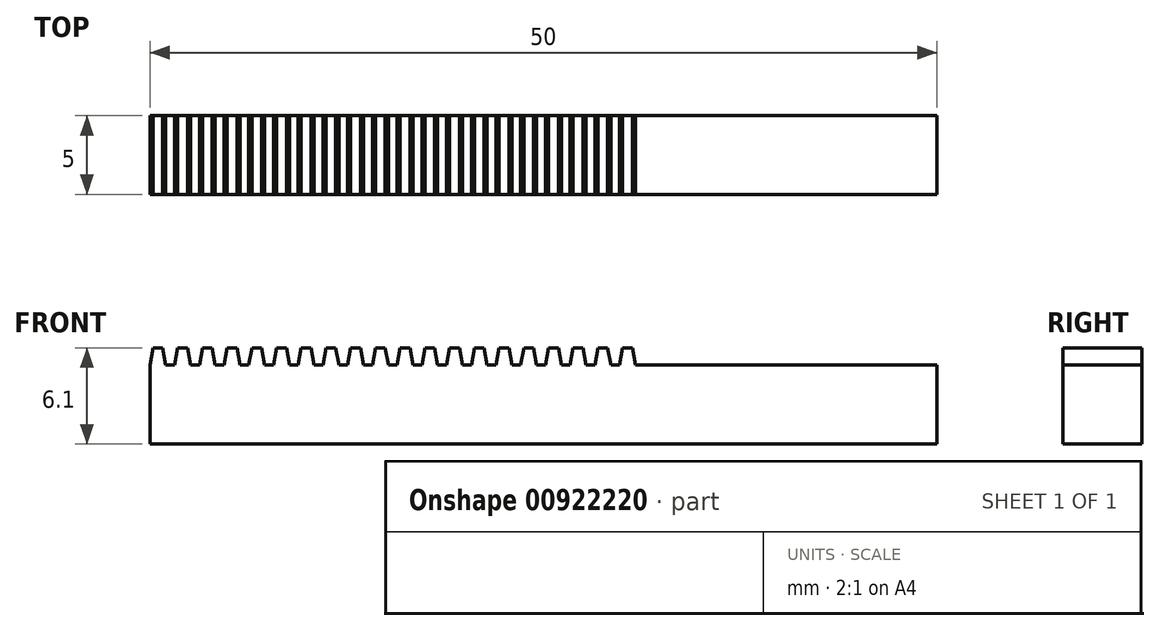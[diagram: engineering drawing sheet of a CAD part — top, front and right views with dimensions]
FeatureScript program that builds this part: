
annotation { "Feature Type Name" : "Feature", "Feature Type Description" : "" }
export const myFeature = defineFeature(function(context is Context, id is Id, definition is map)
    precondition{}
    {
        {
            var Q0;
            Q0=qCreatedBy(makeId("Front.planeOp"),FACE);
            var sketch = newSketch(context, id + "F0", { "sketchPlane" : qUnion([Q0])});
            skLineSegment(sketch, "E0.bottom", {"start": v(0, 0) * mm, "end": v(50, 0) * mm});
            skLineSegment(sketch, "E0.top", {"start": v(0, 5) * mm, "end": v(50, 5) * mm});
            skLineSegment(sketch, "E0.left", {"start": v(0, 0) * mm, "end": v(0, 5) * mm});
            skLineSegment(sketch, "E0.right", {"start": v(50, 0) * mm, "end": v(50, 5) * mm});
            skLineSegment(sketch, "E1", {"start": v(0, 5) * mm, "end": v(1.57, 5) * mm, "construction": true});
            skLineSegment(sketch, "E2", {"start": v(1.57, 5) * mm, "end": v(1.57, 6.1) * mm, "construction": true});
            skLineSegment(sketch, "E3", {"start": v(0, 5) * mm, "end": v(0.2, 6.1) * mm});
            skLineSegment(sketch, "E4", {"start": v(0, 5) * mm, "end": v(1, 5) * mm, "construction": true});
            skLineSegment(sketch, "E5", {"start": v(1, 5) * mm, "end": v(0.82, 6.1) * mm});
            skLineSegment(sketch, "E6", {"start": v(0.2, 6.1) * mm, "end": v(0.82, 6.1) * mm});
            skLineSegment(sketch, "E7.1.0.0", {"start": v(1.57, 5) * mm, "end": v(1.76, 6.1) * mm});
            skLineSegment(sketch, "E7.1.0.1", {"start": v(1.76, 6.1) * mm, "end": v(2.39, 6.1) * mm});
            skLineSegment(sketch, "E7.1.0.2", {"start": v(2.58, 5) * mm, "end": v(2.39, 6.1) * mm});
            skLineSegment(sketch, "E7.2.0.0", {"start": v(3.14, 5) * mm, "end": v(3.33, 6.1) * mm});
            skLineSegment(sketch, "E7.2.0.1", {"start": v(3.33, 6.1) * mm, "end": v(3.96, 6.1) * mm});
            skLineSegment(sketch, "E7.2.0.2", {"start": v(4.15, 5) * mm, "end": v(3.96, 6.1) * mm});
            skLineSegment(sketch, "E8.0.3.0", {"start": v(4.7, 5) * mm, "end": v(4.9, 6.1) * mm});
            skLineSegment(sketch, "E8.3.3.0", {"start": v(4.9, 6.1) * mm, "end": v(5.53, 6.1) * mm});
            skLineSegment(sketch, "E8.6.3.0", {"start": v(5.72, 5) * mm, "end": v(5.53, 6.1) * mm});
            skLineSegment(sketch, "E8.0.4.0", {"start": v(6.28, 5) * mm, "end": v(6.47, 6.1) * mm});
            skLineSegment(sketch, "E8.3.4.0", {"start": v(6.47, 6.1) * mm, "end": v(7.1, 6.1) * mm});
            skLineSegment(sketch, "E8.6.4.0", {"start": v(7.29, 5) * mm, "end": v(7.1, 6.1) * mm});
            skLineSegment(sketch, "E8.0.5.0", {"start": v(7.85, 5) * mm, "end": v(8.04, 6.1) * mm});
            skLineSegment(sketch, "E8.3.5.0", {"start": v(8.04, 6.1) * mm, "end": v(8.67, 6.1) * mm});
            skLineSegment(sketch, "E8.6.5.0", {"start": v(8.86, 5) * mm, "end": v(8.67, 6.1) * mm});
            skLineSegment(sketch, "E8.0.6.0", {"start": v(9.42, 5) * mm, "end": v(9.61, 6.1) * mm});
            skLineSegment(sketch, "E8.3.6.0", {"start": v(9.61, 6.1) * mm, "end": v(10.24, 6.1) * mm});
            skLineSegment(sketch, "E8.6.6.0", {"start": v(10.43, 5) * mm, "end": v(10.24, 6.1) * mm});
            skLineSegment(sketch, "E8.0.7.0", {"start": v(10.99, 5) * mm, "end": v(11.18, 6.1) * mm});
            skLineSegment(sketch, "E8.3.7.0", {"start": v(11.18, 6.1) * mm, "end": v(11.8, 6.1) * mm});
            skLineSegment(sketch, "E8.6.7.0", {"start": v(12, 5) * mm, "end": v(11.8, 6.1) * mm});
            skLineSegment(sketch, "E8.0.8.0", {"start": v(12.56, 5) * mm, "end": v(12.75, 6.1) * mm});
            skLineSegment(sketch, "E8.3.8.0", {"start": v(12.75, 6.1) * mm, "end": v(13.38, 6.1) * mm});
            skLineSegment(sketch, "E8.6.8.0", {"start": v(13.57, 5) * mm, "end": v(13.38, 6.1) * mm});
            skLineSegment(sketch, "E8.0.9.0", {"start": v(14.13, 5) * mm, "end": v(14.32, 6.1) * mm});
            skLineSegment(sketch, "E8.3.9.0", {"start": v(14.32, 6.1) * mm, "end": v(14.95, 6.1) * mm});
            skLineSegment(sketch, "E8.6.9.0", {"start": v(15.14, 5) * mm, "end": v(14.95, 6.1) * mm});
            skLineSegment(sketch, "E8.0.10.0", {"start": v(15.7, 5) * mm, "end": v(15.9, 6.1) * mm});
            skLineSegment(sketch, "E8.3.10.0", {"start": v(15.9, 6.1) * mm, "end": v(16.52, 6.1) * mm});
            skLineSegment(sketch, "E8.6.10.0", {"start": v(16.7, 5) * mm, "end": v(16.52, 6.1) * mm});
            skLineSegment(sketch, "E8.0.11.0", {"start": v(17.27, 5) * mm, "end": v(17.46, 6.1) * mm});
            skLineSegment(sketch, "E8.3.11.0", {"start": v(17.46, 6.1) * mm, "end": v(18.09, 6.1) * mm});
            skLineSegment(sketch, "E8.6.11.0", {"start": v(18.28, 5) * mm, "end": v(18.09, 6.1) * mm});
            skLineSegment(sketch, "E8.0.12.0", {"start": v(18.84, 5) * mm, "end": v(19.03, 6.1) * mm});
            skLineSegment(sketch, "E8.3.12.0", {"start": v(19.03, 6.1) * mm, "end": v(19.66, 6.1) * mm});
            skLineSegment(sketch, "E8.6.12.0", {"start": v(19.85, 5) * mm, "end": v(19.66, 6.1) * mm});
            skLineSegment(sketch, "E8.0.13.0", {"start": v(20.4, 5) * mm, "end": v(20.6, 6.1) * mm});
            skLineSegment(sketch, "E8.3.13.0", {"start": v(20.6, 6.1) * mm, "end": v(21.23, 6.1) * mm});
            skLineSegment(sketch, "E8.6.13.0", {"start": v(21.42, 5) * mm, "end": v(21.23, 6.1) * mm});
            skLineSegment(sketch, "E8.0.14.0", {"start": v(21.98, 5) * mm, "end": v(22.17, 6.1) * mm});
            skLineSegment(sketch, "E8.3.14.0", {"start": v(22.17, 6.1) * mm, "end": v(22.8, 6.1) * mm});
            skLineSegment(sketch, "E8.6.14.0", {"start": v(22.99, 5) * mm, "end": v(22.8, 6.1) * mm});
            skLineSegment(sketch, "E8.0.15.0", {"start": v(23.55, 5) * mm, "end": v(23.74, 6.1) * mm});
            skLineSegment(sketch, "E8.3.15.0", {"start": v(23.74, 6.1) * mm, "end": v(24.37, 6.1) * mm});
            skLineSegment(sketch, "E8.6.15.0", {"start": v(24.56, 5) * mm, "end": v(24.37, 6.1) * mm});
            skLineSegment(sketch, "E8.0.16.0", {"start": v(25.12, 5) * mm, "end": v(25.31, 6.1) * mm});
            skLineSegment(sketch, "E8.3.16.0", {"start": v(25.31, 6.1) * mm, "end": v(25.94, 6.1) * mm});
            skLineSegment(sketch, "E8.6.16.0", {"start": v(26.13, 5) * mm, "end": v(25.94, 6.1) * mm});
            skLineSegment(sketch, "E8.0.17.0", {"start": v(26.69, 5) * mm, "end": v(26.88, 6.1) * mm});
            skLineSegment(sketch, "E8.3.17.0", {"start": v(26.88, 6.1) * mm, "end": v(27.5, 6.1) * mm});
            skLineSegment(sketch, "E8.6.17.0", {"start": v(27.7, 5) * mm, "end": v(27.5, 6.1) * mm});
            skLineSegment(sketch, "E8.0.18.0", {"start": v(28.26, 5) * mm, "end": v(28.45, 6.1) * mm});
            skLineSegment(sketch, "E8.3.18.0", {"start": v(28.45, 6.1) * mm, "end": v(29.08, 6.1) * mm});
            skLineSegment(sketch, "E8.6.18.0", {"start": v(29.27, 5) * mm, "end": v(29.08, 6.1) * mm});
            skLineSegment(sketch, "E8.0.19.0", {"start": v(29.83, 5) * mm, "end": v(30.02, 6.1) * mm});
            skLineSegment(sketch, "E8.3.19.0", {"start": v(30.02, 6.1) * mm, "end": v(30.65, 6.1) * mm});
            skLineSegment(sketch, "E8.6.19.0", {"start": v(30.84, 5) * mm, "end": v(30.65, 6.1) * mm});
            skSolve(sketch);
        }
        {
            var Q0;
            Q0 = qSketchRegion(id + "F0", true);
            extrude(context, id + "F1", {"entities" : qUnion([Q0]), "depth" : 5 * mm, "offsetDistance" : 25 * mm});
        }
    });
